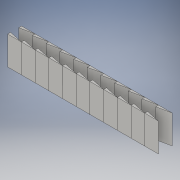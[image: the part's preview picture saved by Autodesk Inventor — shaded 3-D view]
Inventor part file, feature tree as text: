
AUTODESK INVENTOR PART (.ipt)
format: ipt  version: 2016 (Build 200138000, 138)  size: 172,544 bytes
history: native  units: in
note: dims shown in document units (in); Inventor stores cm internally (conversion verified against a paired STEP export)
features: extrude x1, sketch x1
ambient origin geometry x8: Origin, YZ Plane, XZ Plane, XY Plane, X Axis, Y Axis, Z Axis, Center Point
bodies: Body1 (feature_tree)
feature tree (2):
  extrude  "Extrusion2"  Depth=0.074in
  sketch  "Sketch3"  dims[d34=0.0739in d35=0.0158in d36=0.0375in d37=1.182in d38=2.3622in d40=0.148in d41=0.3937in d43=1.0in d45=0.154in d46=0.0in d47=0.7874in d49=0.074in d50=0.3937in d52=1.0in]
